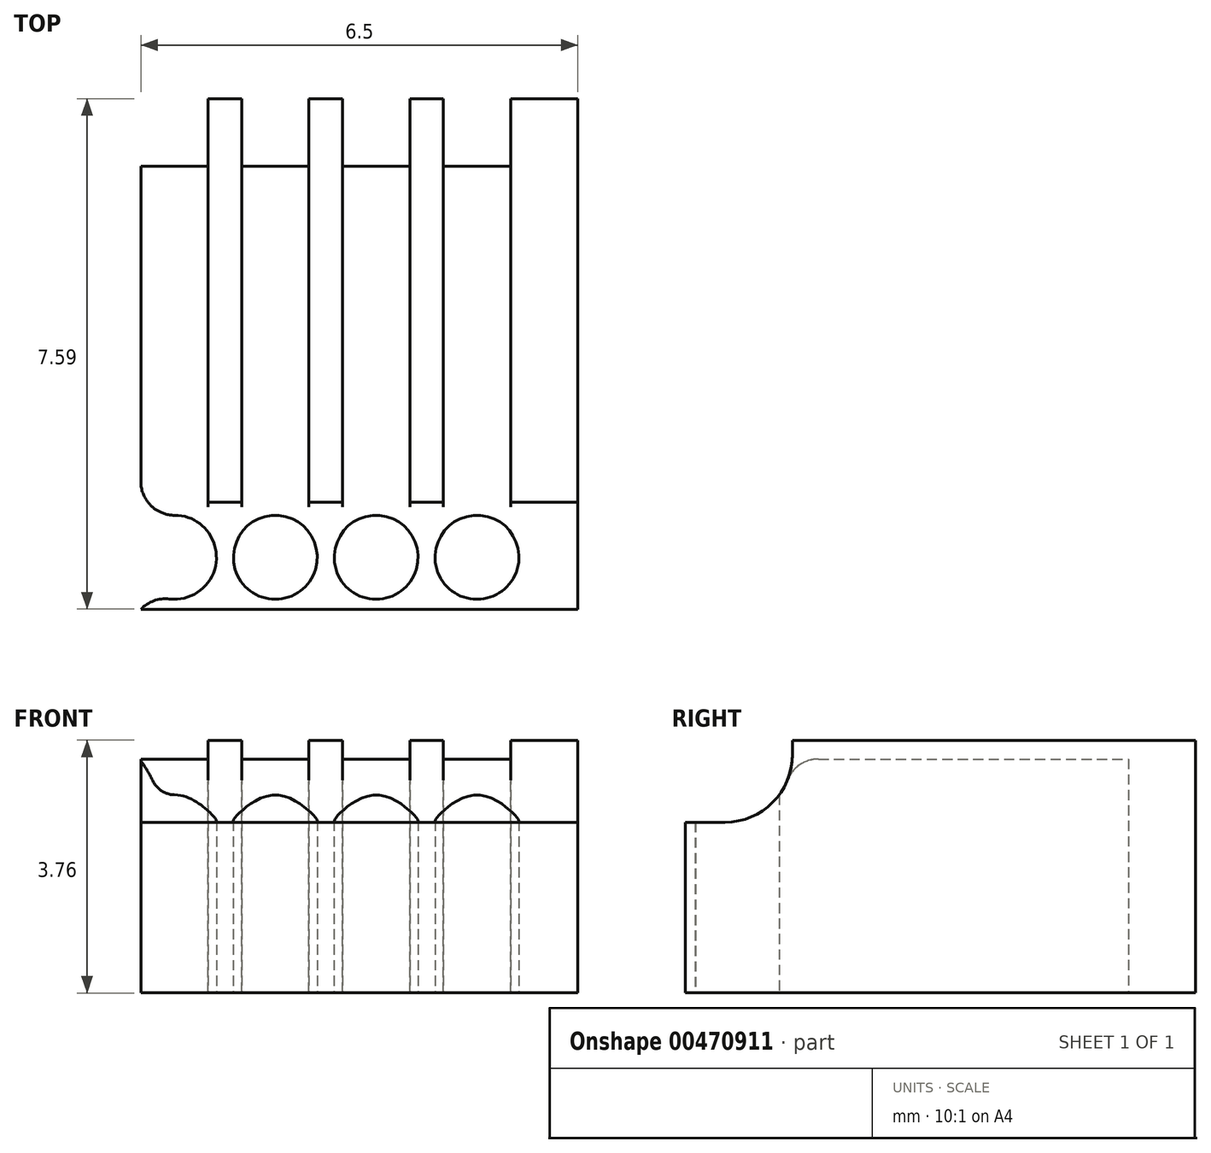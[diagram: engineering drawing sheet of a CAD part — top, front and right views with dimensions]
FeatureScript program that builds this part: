
annotation { "Feature Type Name" : "Feature", "Feature Type Description" : "" }
export const myFeature = defineFeature(function(context is Context, id is Id, definition is map)
    precondition{}
    {
        {
            var Q0;
            Q0=qCreatedBy(makeId("Front.planeOp"),FACE);
            var sketch = newSketch(context, id + "F0", { "sketchPlane" : qUnion([Q0])});
            skLineSegment(sketch, "E0.bottom", {"start": v(3.25, -1.87) * mm, "end": v(-3.25, -1.88) * mm});
            skLineSegment(sketch, "E0.top", {"start": v(3.25, 1.88) * mm, "end": v(-3.25, 1.88) * mm});
            skLineSegment(sketch, "E0.left", {"start": v(3.25, -1.87) * mm, "end": v(3.25, 1.88) * mm});
            skLineSegment(sketch, "E0.right", {"start": v(-3.25, -1.87) * mm, "end": v(-3.25, 1.88) * mm});
            skPoint(sketch, "E0.middle", {"position": v(0, 0) * mm});
            skLineSegment(sketch, "E1", {"start": v(-2.75, 1.6) * mm, "end": v(-2.75, 4.29) * mm, "construction": true});
            skLineSegment(sketch, "E2.bottom", {"start": v(-3.25, 1.6) * mm, "end": v(-2.25, 1.6) * mm});
            skLineSegment(sketch, "E2.top", {"start": v(-3.25, 4.29) * mm, "end": v(-2.25, 4.29) * mm});
            skLineSegment(sketch, "E2.left", {"start": v(-3.25, 1.6) * mm, "end": v(-3.25, 4.29) * mm});
            skLineSegment(sketch, "E2.right", {"start": v(-2.25, 1.6) * mm, "end": v(-2.25, 4.29) * mm});
            skLineSegment(sketch, "E3.1.0.0", {"start": v(-1.75, 1.6) * mm, "end": v(-1.75, 4.29) * mm});
            skLineSegment(sketch, "E3.1.0.1", {"start": v(-0.75, 1.6) * mm, "end": v(-0.75, 4.29) * mm});
            skLineSegment(sketch, "E3.1.0.2", {"start": v(-1.75, 1.6) * mm, "end": v(-0.75, 1.6) * mm});
            skLineSegment(sketch, "E3.1.0.3", {"start": v(-1.75, 4.29) * mm, "end": v(-0.75, 4.29) * mm});
            skLineSegment(sketch, "E3.2.0.0", {"start": v(-0.25, 1.6) * mm, "end": v(-0.25, 4.29) * mm});
            skLineSegment(sketch, "E3.2.0.1", {"start": v(0.75, 1.6) * mm, "end": v(0.75, 4.29) * mm});
            skLineSegment(sketch, "E3.2.0.2", {"start": v(-0.25, 1.6) * mm, "end": v(0.75, 1.6) * mm});
            skLineSegment(sketch, "E3.2.0.3", {"start": v(-0.25, 4.29) * mm, "end": v(0.75, 4.29) * mm});
            skLineSegment(sketch, "E3.3.0.0", {"start": v(1.25, 1.6) * mm, "end": v(1.25, 4.29) * mm});
            skLineSegment(sketch, "E3.3.0.1", {"start": v(2.25, 1.6) * mm, "end": v(2.25, 4.29) * mm});
            skLineSegment(sketch, "E3.3.0.2", {"start": v(1.25, 1.6) * mm, "end": v(2.25, 1.6) * mm});
            skLineSegment(sketch, "E3.3.0.3", {"start": v(1.25, 4.29) * mm, "end": v(2.25, 4.29) * mm});
            skLineSegment(sketch, "E3.direction1", {"start": v(-3.25, 1.6) * mm, "end": v(-1.75, 1.6) * mm, "construction": true});
            skLineSegment(sketch, "E4", {"start": v(-2.25, 1.6) * mm, "end": v(-2.25, -1.88) * mm});
            skLineSegment(sketch, "E5", {"start": v(-0.75, 1.6) * mm, "end": v(-0.75, -1.88) * mm});
            skLineSegment(sketch, "E6", {"start": v(-1.75, 1.6) * mm, "end": v(-1.75, -1.88) * mm});
            skLineSegment(sketch, "E7", {"start": v(2.25, 1.6) * mm, "end": v(2.25, -1.87) * mm});
            skLineSegment(sketch, "E8", {"start": v(1.25, 1.6) * mm, "end": v(1.25, -1.87) * mm});
            skLineSegment(sketch, "E9", {"start": v(0.75, 1.6) * mm, "end": v(0.75, -1.87) * mm});
            skLineSegment(sketch, "E10", {"start": v(-0.25, 1.6) * mm, "end": v(-0.25, -1.87) * mm});
            skSolve(sketch);
        }
        {
            var Q0;
            Q0=makeQuery(id+"F0.imprint","IMPRINT",FACE,{"disambiguationData":[TD([[makeQuery(id+"F0.imprint","IMPRINT",EDGE,{"derivedFrom":sQuery(id+"F0.wireOp",EDGE,"E0.bottom")}),-1.0]])]});
            var Q1;
            {var subQ0=sQuery(id+"F0.wireOp",EDGE,"E4");Q1=makeQuery(id+"F0.imprint","IMPRINT",FACE,{"disambiguationData":[TD([[makeQuery(id+"F0.imprint","IMPRINT",EDGE,{"derivedFrom":subQ0}),1.0]])]});}
            var Q2;
            {var subQ4=sQuery(id+"F0.wireOp",EDGE,"E5");Q2=makeQuery(id+"F0.imprint","IMPRINT",FACE,{"disambiguationData":[TD([[makeQuery(id+"F0.imprint","IMPRINT",EDGE,{"derivedFrom":subQ4}),1.0]])]});}
            var Q3;
            {var subQ0=sQuery(id+"F0.wireOp",EDGE,"E8");Q3=makeQuery(id+"F0.imprint","IMPRINT",FACE,{"disambiguationData":[TD([[makeQuery(id+"F0.imprint","IMPRINT",EDGE,{"derivedFrom":subQ0}),-1.0]])]});}
            var Q4;
            {var subQ0=sQuery(id+"F0.wireOp",EDGE,"E0.left");Q4=makeQuery(id+"F0.imprint","IMPRINT",FACE,{"disambiguationData":[TD([[makeQuery(id+"F0.imprint","IMPRINT",EDGE,{"derivedFrom":subQ0}),1.0]])]});}
            extrude(context, id + "F1", {"entities" : qUnion([Q0, Q1, Q2, Q3, Q4]), "depth" : 6 * mm});
        }
        {
            var Q0;
            Q0=makeQuery(id+"F0.imprint","IMPRINT",FACE,{"disambiguationData":[TD([[makeQuery(id+"F0.imprint","IMPRINT",EDGE,{"derivedFrom":sQuery(id+"F0.wireOp",EDGE,"E3.3.0.2")}),-1.0]])]});
            var Q1;
            Q1=makeQuery(id+"F0.imprint","IMPRINT",FACE,{"disambiguationData":[TD([[makeQuery(id+"F0.imprint","IMPRINT",EDGE,{"derivedFrom":sQuery(id+"F0.wireOp",EDGE,"E3.2.0.2")}),-1.0]])]});
            var Q2;
            Q2=makeQuery(id+"F0.imprint","IMPRINT",FACE,{"disambiguationData":[TD([[makeQuery(id+"F0.imprint","IMPRINT",EDGE,{"derivedFrom":sQuery(id+"F0.wireOp",EDGE,"E3.1.0.2")}),-1.0]])]});
            var Q3;
            {var subQ0=sQuery(id+"F0.wireOp",EDGE,"E0.right");Q3=makeQuery(id+"F0.imprint","IMPRINT",FACE,{"disambiguationData":[TD([[makeQuery(id+"F0.imprint","IMPRINT",EDGE,{"derivedFrom":subQ0}),-1.0]])]});}
            extrude(context, id + "F2", {"entities" : qUnion([Q0, Q1, Q2, Q3]), "operationType" : NewBodyOperationType.REMOVE, "depth" : 1 * mm});
        }
        {
            var Q0;
            Q0=qCreatedBy(makeId("Top.planeOp"),FACE);
            var sketch = newSketch(context, id + "F3", { "sketchPlane" : qUnion([Q0])});
            skLineSegment(sketch, "E11.bottom", {"start": v(-3.25, -6) * mm, "end": v(3.25, -6) * mm});
            skLineSegment(sketch, "E11.top", {"start": v(-3.25, -7.6) * mm, "end": v(3.25, -7.6) * mm});
            skLineSegment(sketch, "E11.left", {"start": v(-3.25, -6) * mm, "end": v(-3.25, -7.6) * mm});
            skLineSegment(sketch, "E11.right", {"start": v(3.25, -6) * mm, "end": v(3.25, -7.6) * mm});
            skLineSegment(sketch, "E12", {"start": v(-3.25, 0.92) * mm, "end": v(-3.25, -10.1) * mm, "construction": true});
            skLineSegment(sketch, "E13", {"start": v(3.25, 1.38) * mm, "end": v(3.25, -10.23) * mm, "construction": true});
            skCircle(sketch, "E14", {"center": v(-2.75, -6.82) * mm, "radius": 0.62 * mm});
            skLineSegment(sketch, "E15", {"start": v(-3.25, -6) * mm, "end": v(-2.25, -6) * mm, "construction": true});
            skLineSegment(sketch, "E16", {"start": v(-2.25, -4.44) * mm, "end": v(-2.25, -10.1) * mm, "construction": true});
            skPoint(sketch, "E17", {"position": v(-2.75, -6) * mm});
            skCircle(sketch, "E18.1.0.0", {"center": v(-1.25, -6.82) * mm, "radius": 0.62 * mm});
            skCircle(sketch, "E18.2.0.0", {"center": v(0.25, -6.82) * mm, "radius": 0.62 * mm});
            skCircle(sketch, "E18.3.0.0", {"center": v(1.75, -6.82) * mm, "radius": 0.62 * mm});
            skLineSegment(sketch, "E18.direction1", {"start": v(-2.75, -6.75) * mm, "end": v(-1.25, -6.75) * mm, "construction": true});
            skSolve(sketch);
        }
        {
            var Q0;
            {var subQ4=sQuery(id+"F3.wireOp",EDGE,"E11.bottom");Q0=makeQuery(id+"F3.imprint","IMPRINT",FACE,{"disambiguationData":[TD([[makeQuery(id+"F3.imprint","IMPRINT",EDGE,{"derivedFrom":subQ4}),-1.0]])]});}
            extrude(context, id + "F4", {"entities" : qUnion([Q0]), "operationType" : NewBodyOperationType.ADD, "endBound" : BoundingType.SYMMETRIC, "depth" : 1.32 * mm});
        }
        {
            var Q0;
            {var subQ4=sQuery(id+"F3.wireOp",EDGE,"E11.bottom");Q0=makeQuery(id+"F3.imprint","IMPRINT",FACE,{"disambiguationData":[TD([[makeQuery(id+"F3.imprint","IMPRINT",EDGE,{"derivedFrom":subQ4}),-1.0]])]});}
            extrude(context, id + "F5", {"entities" : qUnion([Q0]), "operationType" : NewBodyOperationType.ADD, "oppositeDirection" : true, "depth" : 1.88 * mm});
        }
        {
            var Q0;
            Q0=makeQuery(id+"F4.opExtrude","CAP_EDGE",EDGE,{"disambiguationData":[OSD([sQuery(id+"F3.wireOp",EDGE,"E11.bottom")])],"isStart":false});
            fillet(context, id + "F6", {"entities" : qUnion([Q0]), "radius" : 1 * mm, "tangentPropagation" : true, "allowEdgeOverflow" : false});
        }
        {
            var Q0;
            Q0=makeQuery(id+"F6.opFillet","BLEND_EDGE",EDGE,{"blendedFrom":[makeQuery(id+"F4.opExtrude","CAP_EDGE",EDGE,{"disambiguationData":[OSD([sQuery(id+"F3.wireOp",EDGE,"E11.bottom")])],"isStart":false}),makeQuery(id+"F1.opExtrude","SWEPT_FACE",FACE,{"disambiguationData":[OSD([sQuery(id+"F0.wireOp",EDGE,"E2.bottom")])]})],"blendedInto":[makeQuery(id+"F1.opExtrude","SWEPT_FACE",FACE,{"disambiguationData":[OSD([sQuery(id+"F0.wireOp",EDGE,"E2.bottom")])]})]});
            var Q1;
            Q1=makeQuery(id+"F6.opFillet","BLEND_EDGE",EDGE,{"blendedFrom":[makeQuery(id+"F4.opExtrude","CAP_EDGE",EDGE,{"disambiguationData":[OSD([sQuery(id+"F3.wireOp",EDGE,"E11.bottom")])],"isStart":false}),makeQuery(id+"F1.opExtrude","SWEPT_FACE",FACE,{"disambiguationData":[OSD([sQuery(id+"F0.wireOp",EDGE,"E3.1.0.2")])]})],"blendedInto":[makeQuery(id+"F1.opExtrude","SWEPT_FACE",FACE,{"disambiguationData":[OSD([sQuery(id+"F0.wireOp",EDGE,"E3.1.0.2")])]})]});
            var Q2;
            Q2=makeQuery(id+"F6.opFillet","BLEND_EDGE",EDGE,{"blendedFrom":[makeQuery(id+"F4.opExtrude","CAP_EDGE",EDGE,{"disambiguationData":[OSD([sQuery(id+"F3.wireOp",EDGE,"E11.bottom")])],"isStart":false}),makeQuery(id+"F1.opExtrude","SWEPT_FACE",FACE,{"disambiguationData":[OSD([sQuery(id+"F0.wireOp",EDGE,"E3.2.0.2")])]})],"blendedInto":[makeQuery(id+"F1.opExtrude","SWEPT_FACE",FACE,{"disambiguationData":[OSD([sQuery(id+"F0.wireOp",EDGE,"E3.2.0.2")])]})]});
            var Q3;
            Q3=makeQuery(id+"F6.opFillet","BLEND_EDGE",EDGE,{"blendedFrom":[makeQuery(id+"F4.opExtrude","CAP_EDGE",EDGE,{"disambiguationData":[OSD([sQuery(id+"F3.wireOp",EDGE,"E11.bottom")])],"isStart":false}),makeQuery(id+"F1.opExtrude","SWEPT_FACE",FACE,{"disambiguationData":[OSD([sQuery(id+"F0.wireOp",EDGE,"E3.3.0.2")])]})],"blendedInto":[makeQuery(id+"F1.opExtrude","SWEPT_FACE",FACE,{"disambiguationData":[OSD([sQuery(id+"F0.wireOp",EDGE,"E3.3.0.2")])]})]});
            var Q4;
            {var subQ0=sQuery(id+"F3.wireOp",EDGE,"E14");var subQ1=sQuery(id+"F3.wireOp",EDGE,"E11.left");var subQ2=makeQuery(id+"F3.imprint","INTERSECT",VERTEX,{"disambiguationData":[OD(0.0)],"derivedFrom":[subQ1,subQ0]});Q4=makeQuery(id+"F5.boolean.opBoolean","MERGE",EDGE,{"derivedFrom":[makeQuery(id+"F4.opExtrude","SWEPT_EDGE",EDGE,{"disambiguationData":[OSD([subQ1,subQ0]),TDD([subQ2])]}),makeQuery(id+"F5.opExtrude","SWEPT_EDGE",EDGE,{"disambiguationData":[OSD([subQ1,subQ0]),TDD([subQ2])]})]});}
            var Q5;
            {var subQ0=sQuery(id+"F3.wireOp",EDGE,"E14");var subQ1=sQuery(id+"F3.wireOp",EDGE,"E11.left");var subQ2=makeQuery(id+"F3.imprint","INTERSECT",VERTEX,{"disambiguationData":[OD(1.0)],"derivedFrom":[subQ1,subQ0]});Q5=makeQuery(id+"F5.boolean.opBoolean","MERGE",EDGE,{"derivedFrom":[makeQuery(id+"F4.opExtrude","SWEPT_EDGE",EDGE,{"disambiguationData":[OSD([subQ1,subQ0]),TDD([subQ2])]}),makeQuery(id+"F5.opExtrude","SWEPT_EDGE",EDGE,{"disambiguationData":[OSD([subQ1,subQ0]),TDD([subQ2])]})]});}
            var Q6;
            Q6=makeQuery(id+"F2.boolean.opBoolean","COPY",EDGE,{"derivedFrom":makeQuery(id+"F2.opExtrude","CAP_EDGE",EDGE,{"disambiguationData":[OSD([sQuery(id+"F0.wireOp",EDGE,"E3.3.0.2")])],"isStart":false})});
            var Q7;
            Q7=makeQuery(id+"F2.boolean.opBoolean","COPY",EDGE,{"derivedFrom":makeQuery(id+"F2.opExtrude","CAP_EDGE",EDGE,{"disambiguationData":[OSD([sQuery(id+"F0.wireOp",EDGE,"E3.2.0.2")])],"isStart":false})});
            var Q8;
            Q8=makeQuery(id+"F2.boolean.opBoolean","COPY",EDGE,{"derivedFrom":makeQuery(id+"F2.opExtrude","CAP_EDGE",EDGE,{"disambiguationData":[OSD([sQuery(id+"F0.wireOp",EDGE,"E3.1.0.2")])],"isStart":false})});
            var Q9;
            Q9=makeQuery(id+"F2.boolean.opBoolean","COPY",EDGE,{"derivedFrom":makeQuery(id+"F2.opExtrude","CAP_EDGE",EDGE,{"disambiguationData":[OSD([sQuery(id+"F0.wireOp",EDGE,"E2.bottom")])],"isStart":false})});
            fillet(context, id + "F7", {"entities" : qUnion([Q0, Q1, Q2, Q3, Q4, Q5, Q6, Q7, Q8, Q9]), "radius" : 0.5 * mm, "tangentPropagation" : true, "allowEdgeOverflow" : false});
        }
    });
